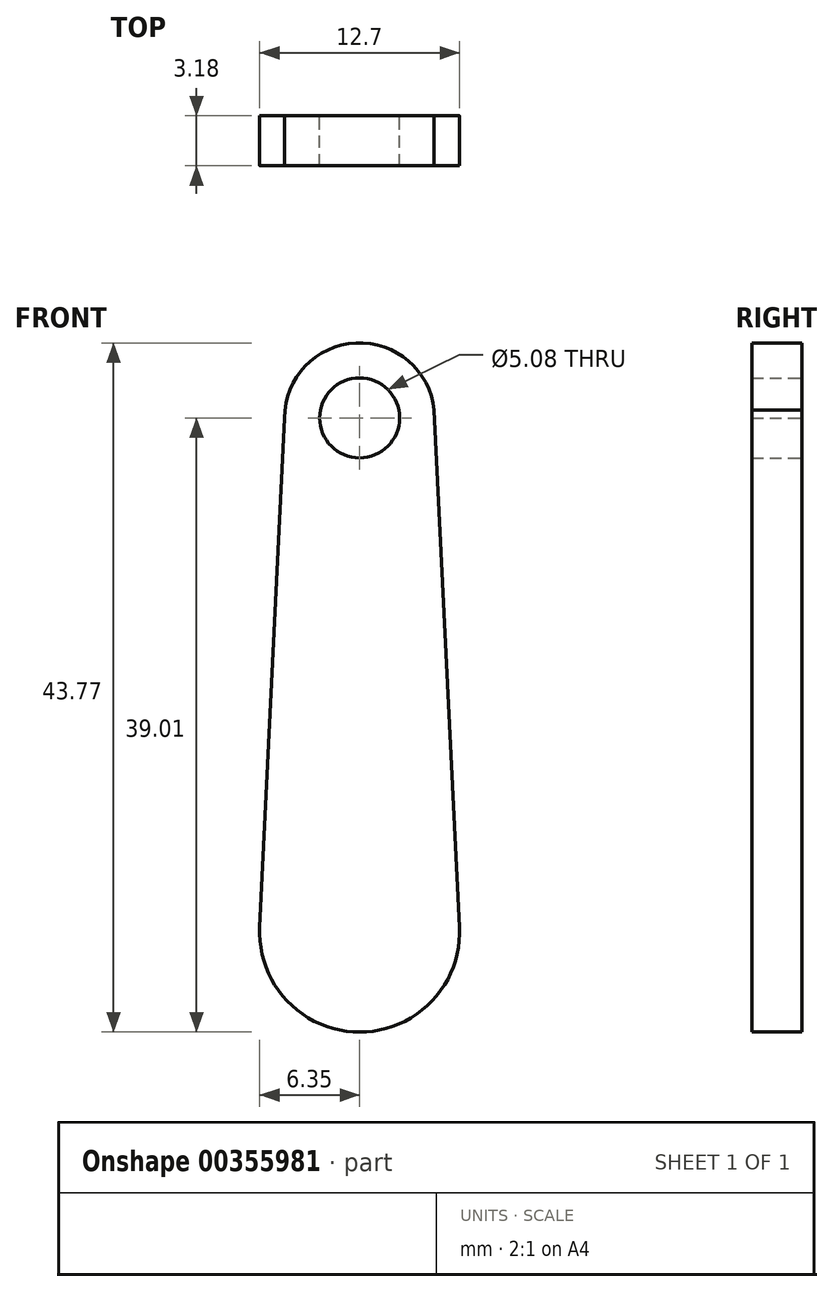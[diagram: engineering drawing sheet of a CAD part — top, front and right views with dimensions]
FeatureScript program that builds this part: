
annotation { "Feature Type Name" : "Feature", "Feature Type Description" : "" }
export const myFeature = defineFeature(function(context is Context, id is Id, definition is map)
    precondition{}
    {
        {
            var Q0;
            Q0=qCreatedBy(makeId("Front.planeOp"),FACE);
            var sketch = newSketch(context, id + "F0", { "sketchPlane" : qUnion([Q0])});
            skArc(sketch, "E0", {"start": v(-6.34, 0.3) * mm, "mid": v(0, -6.35) * mm, "end": v(6.34, 0.3) * mm});
            skArc(sketch, "E1", {"start": v(4.76, 32.64) * mm, "mid": v(0.01, 37.42) * mm, "end": v(-4.76, 32.66) * mm});
            skLineSegment(sketch, "E2", {"start": v(-4.76, 32.66) * mm, "end": v(-6.36, 0) * mm});
            skLineSegment(sketch, "E3", {"start": v(4.74, 33.15) * mm, "end": v(6.36, 0) * mm});
            skCircle(sketch, "E4", {"center": v(0, 32.66) * mm, "radius": 2.54 * mm});
            skSolve(sketch);
        }
        {
            var Q0;
            {var subQ5=sQuery(id+"F0.wireOp",EDGE,"E0");Q0=makeQuery(id+"F0.imprint","IMPRINT",FACE,{"disambiguationData":[TD([[makeQuery(id+"F0.imprint","IMPRINT",EDGE,{"derivedFrom":subQ5}),1.0]])]});}
            extrude(context, id + "F1", {"entities" : qUnion([Q0]), "depth" : 3.17 * mm});
        }
    });
